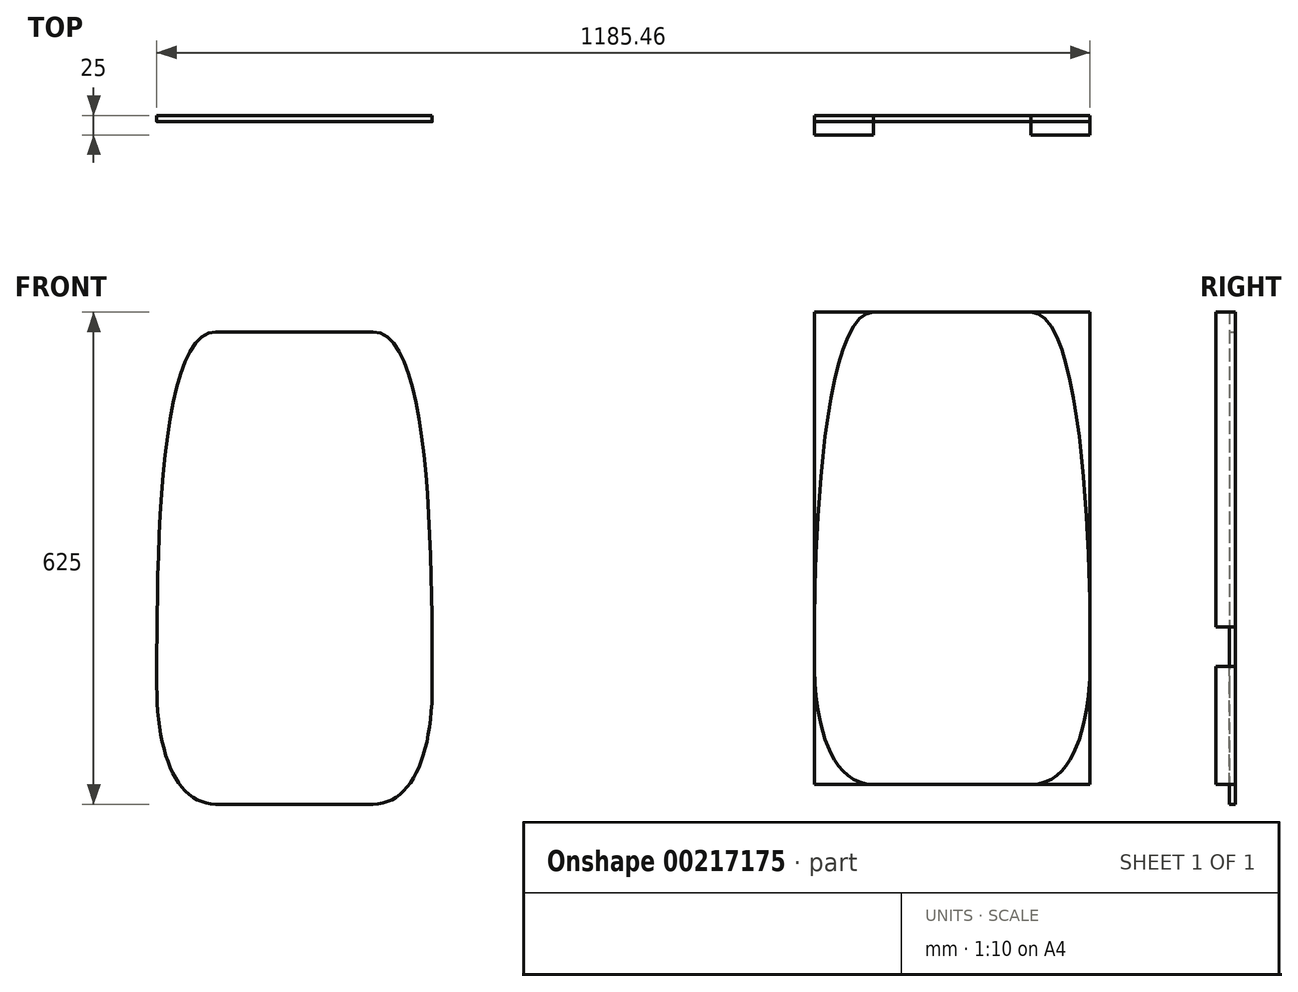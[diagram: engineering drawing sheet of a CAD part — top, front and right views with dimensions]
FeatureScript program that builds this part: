
annotation { "Feature Type Name" : "Feature", "Feature Type Description" : "" }
export const myFeature = defineFeature(function(context is Context, id is Id, definition is map)
    precondition{}
    {
        {
            var Q0;
            Q0=qCreatedBy(makeId("Front.planeOp"),FACE);
            var sketch = newSketch(context, id + "F0", { "sketchPlane" : qUnion([Q0])});
            skPoint(sketch, "E0.middle", {"position": v(751, 0) * mm});
            skPoint(sketch, "E1", {"position": v(1010.46, -75) * mm});
            skFitSpline(sketch, "E2", {"points": [v(935.46, 325) * mm, v(1010.46, -75) * mm], "startDerivative": vector(225, 0) * mm, "endDerivative": vector(0, -30) * mm});
            skFitSpline(sketch, "E3.MirrorCS", {"points": [v(735.46, 325) * mm, v(660.46, -75) * mm], "startDerivative": vector(-225, 0) * mm, "endDerivative": vector(0, -30) * mm});
            skFitSpline(sketch, "E4.MirrorCS", {"points": [v(735.46, -275) * mm, v(660.46, -125) * mm], "startDerivative": vector(-225, 0) * mm, "endDerivative": vector(0, 30) * mm});
            skFitSpline(sketch, "E5.MirrorCS", {"points": [v(935.46, -275) * mm, v(1010.46, -125) * mm], "startDerivative": vector(225, 0) * mm, "endDerivative": vector(0, 30) * mm});
            skLineSegment(sketch, "E6", {"start": v(735.46, -275) * mm, "end": v(935.46, -275) * mm});
            skLineSegment(sketch, "E7", {"start": v(660.46, -275) * mm, "end": v(660.46, 325) * mm});
            skLineSegment(sketch, "E8", {"start": v(1010.46, 325) * mm, "end": v(1010.46, -275) * mm});
            skLineSegment(sketch, "E9", {"start": v(660.46, -275) * mm, "end": v(1010.46, -275) * mm});
            skLineSegment(sketch, "E10", {"start": v(660.46, 325) * mm, "end": v(1010.46, 325) * mm});
            skPoint(sketch, "E11.endSnap0", {"position": v(660.46, 25) * mm});
            skSolve(sketch);
        }
        {
            var Q0;
            {var subQ3=sQuery(id+"F0.wireOp",EDGE,"E2");Q0=makeQuery(id+"F0.imprint","IMPRINT",FACE,{"disambiguationData":[TD([[makeQuery(id+"F0.imprint","IMPRINT",EDGE,{"derivedFrom":subQ3}),-1.0]])]});}
            extrude(context, id + "F1", {"entities" : qUnion([Q0]), "depth" : 8 * mm});
        }
        {
            var Q0;
            {var subQ0=sQuery(id+"F0.wireOp",EDGE,"E5.MirrorCS");Q0=makeQuery(id+"F0.imprint","IMPRINT",FACE,{"disambiguationData":[TD([[makeQuery(id+"F0.imprint","IMPRINT",EDGE,{"derivedFrom":subQ0}),-1.0]])]});}
            var Q1;
            {var subQ0=sQuery(id+"F0.wireOp",EDGE,"E4.MirrorCS");Q1=makeQuery(id+"F0.imprint","IMPRINT",FACE,{"disambiguationData":[TD([[makeQuery(id+"F0.imprint","IMPRINT",EDGE,{"derivedFrom":subQ0}),1.0]])]});}
            var Q2;
            {var subQ0=sQuery(id+"F0.wireOp",EDGE,"E3.MirrorCS");Q2=makeQuery(id+"F0.imprint","IMPRINT",FACE,{"disambiguationData":[TD([[makeQuery(id+"F0.imprint","IMPRINT",EDGE,{"derivedFrom":subQ0}),-1.0]])]});}
            var Q3;
            {var subQ0=sQuery(id+"F0.wireOp",EDGE,"E2");Q3=makeQuery(id+"F0.imprint","IMPRINT",FACE,{"disambiguationData":[TD([[makeQuery(id+"F0.imprint","IMPRINT",EDGE,{"derivedFrom":subQ0}),1.0]])]});}
            extrude(context, id + "F2", {"entities" : qUnion([Q0, Q1, Q2, Q3]), "depth" : 25 * mm});
        }
        {
            var Q0;
            Q0=qCreatedBy(makeId("Front.planeOp"),FACE);
            var sketch = newSketch(context, id + "F3", { "sketchPlane" : qUnion([Q0])});
            skLineSegment(sketch, "E12", {"start": v(-142.8, -532.49) * mm, "end": v(257.2, -532.49) * mm});
            skLineSegment(sketch, "E13", {"start": v(257.2, -532.49) * mm, "end": v(257.2, -475.49) * mm});
            skLineSegment(sketch, "E14", {"start": v(-142.8, -532.49) * mm, "end": v(-142.8, -522.49) * mm});
            skFitSpline(sketch, "E15", {"points": [v(257.2, -475.49) * mm, v(-142.8, -522.49) * mm], "startDerivative": vector(0, -85.5) * mm, "endDerivative": vector(-224.92, -0.2) * mm});
            skLineSegment(sketch, "E16.bottom", {"start": v(-175, 300) * mm, "end": v(175, 300) * mm});
            skLineSegment(sketch, "E16.top", {"start": v(-175, -300) * mm, "end": v(175, -300) * mm});
            skLineSegment(sketch, "E16.left", {"start": v(-175, 300) * mm, "end": v(-175, -300) * mm});
            skLineSegment(sketch, "E16.right", {"start": v(175, 300) * mm, "end": v(175, -300) * mm});
            skPoint(sketch, "E16.middle", {"position": v(0, 0) * mm});
            skPoint(sketch, "E17", {"position": v(-100, 300) * mm});
            skPoint(sketch, "E18", {"position": v(-100, -300) * mm});
            skPoint(sketch, "E19", {"position": v(-175, -150) * mm});
            skFitSpline(sketch, "E20", {"points": [v(-100, 300) * mm, v(-175, -150) * mm], "startDerivative": vector(-225, 0) * mm, "endDerivative": vector(0, -450) * mm});
            skFitSpline(sketch, "E21", {"points": [v(-175, -150) * mm, v(-100, -300) * mm], "startDerivative": vector(0, -254.33) * mm, "endDerivative": vector(150.19, 0) * mm});
            skLineSegment(sketch, "E22", {"start": v(0, 0) * mm, "end": v(0, 135.5) * mm});
            skFitSpline(sketch, "E23.MirrorCS", {"points": [v(100, 300) * mm, v(175, -150) * mm], "startDerivative": vector(225, 0) * mm, "endDerivative": vector(0, -450) * mm});
            skFitSpline(sketch, "E24.MirrorCS", {"points": [v(175, -150) * mm, v(100, -300) * mm], "startDerivative": vector(0, -254.33) * mm, "endDerivative": vector(-150.19, 0) * mm});
            skPoint(sketch, "E25", {"position": v(0, -300) * mm});
            skSolve(sketch);
        }
        {
            var Q0;
            {var subQ1=sQuery(id+"F3.wireOp",EDGE,"E20");Q0=makeQuery(id+"F3.imprint","IMPRINT",FACE,{"disambiguationData":[TD([[makeQuery(id+"F3.imprint","IMPRINT",EDGE,{"derivedFrom":subQ1}),1.0]])]});}
            extrude(context, id + "F4", {"entities" : qUnion([Q0]), "depth" : 8 * mm});
        }
    });
